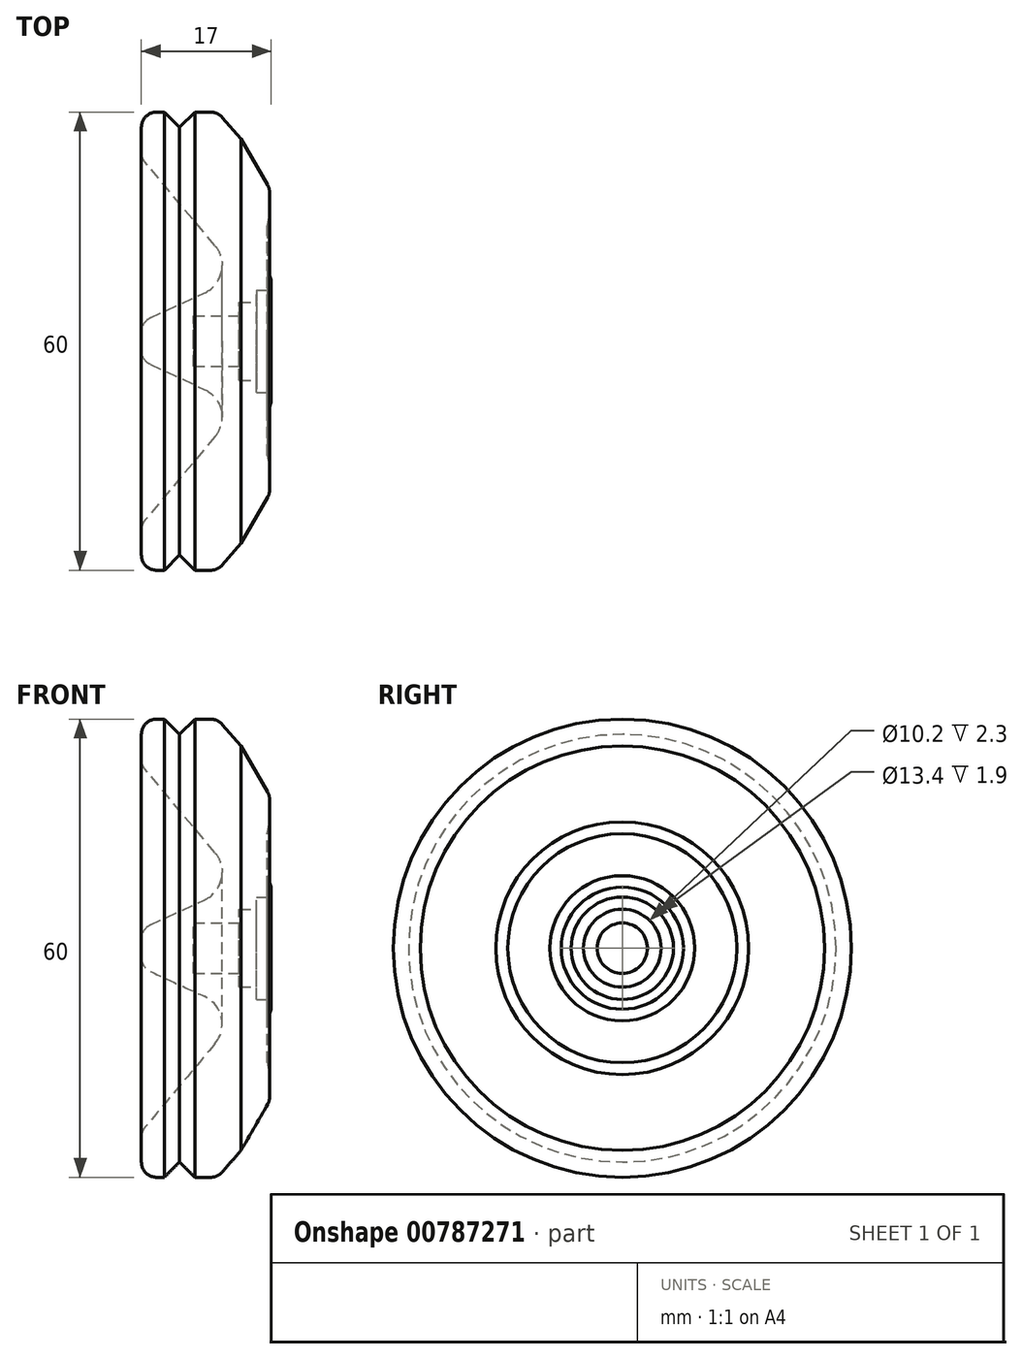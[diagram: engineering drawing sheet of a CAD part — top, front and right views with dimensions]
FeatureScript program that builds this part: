
annotation { "Feature Type Name" : "Feature", "Feature Type Description" : "" }
export const myFeature = defineFeature(function(context is Context, id is Id, definition is map)
    precondition{}
    {
        {
            var Q0;
            Q0=qCreatedBy(makeId("Front.planeOp"),FACE);
            var sketch = newSketch(context, id + "F0", { "sketchPlane" : qUnion([Q0])});
            skLineSegment(sketch, "E0", {"start": v(0, 0) * mm, "end": v(0, 1.22) * mm});
            skLineSegment(sketch, "E1", {"start": v(1.16, 3.04) * mm, "end": v(8.25, 6.3) * mm});
            skLineSegment(sketch, "E2", {"start": v(9.64, 12.5) * mm, "end": v(0.47, 23.44) * mm});
            skLineSegment(sketch, "E3", {"start": v(0, 24.73) * mm, "end": v(0, 28) * mm});
            skLineSegment(sketch, "E4", {"start": v(2, 30) * mm, "end": v(3, 30) * mm});
            skLineSegment(sketch, "E5", {"start": v(3, 30) * mm, "end": v(5, 28) * mm});
            skLineSegment(sketch, "E6", {"start": v(5, 28) * mm, "end": v(7, 30) * mm});
            skLineSegment(sketch, "E7", {"start": v(7, 30) * mm, "end": v(9.09, 30) * mm});
            skLineSegment(sketch, "E8", {"start": v(10.6, 29.31) * mm, "end": v(13.06, 26.48) * mm});
            skLineSegment(sketch, "E9", {"start": v(13.06, 26.48) * mm, "end": v(16.53, 20.46) * mm});
            skLineSegment(sketch, "E10", {"start": v(16.8, 19.46) * mm, "end": v(16.8, 16.55) * mm});
            skLineSegment(sketch, "E11", {"start": v(16.8, 16.55) * mm, "end": v(16.5, 15) * mm});
            skLineSegment(sketch, "E12", {"start": v(16.5, 15) * mm, "end": v(16.5, 9.5) * mm});
            skLineSegment(sketch, "E13", {"start": v(16.5, 9.5) * mm, "end": v(17, 8) * mm});
            skLineSegment(sketch, "E14", {"start": v(17, 8) * mm, "end": v(17, 6.7) * mm});
            skLineSegment(sketch, "E15", {"start": v(17, 6.7) * mm, "end": v(15.1, 6.7) * mm});
            skLineSegment(sketch, "E16", {"start": v(15.1, 6.7) * mm, "end": v(15.1, 5.1) * mm});
            skLineSegment(sketch, "E17", {"start": v(15.1, 5.1) * mm, "end": v(12.8, 5.1) * mm});
            skLineSegment(sketch, "E18", {"start": v(12.8, 5.1) * mm, "end": v(12.8, 3.3) * mm});
            skLineSegment(sketch, "E19", {"start": v(12.8, 3.3) * mm, "end": v(6.8, 3.3) * mm});
            skLineSegment(sketch, "E20", {"start": v(6.8, 3.3) * mm, "end": v(6.8, 0) * mm});
            skLineSegment(sketch, "E21", {"start": v(6.8, 0) * mm, "end": v(0, 0) * mm});
            skPoint(sketch, "E22.visualSharp", {"position": v(0, 30) * mm});
            skArc(sketch, "E22.filletArc", {"start": v(2, 30) * mm, "mid": v(0.59, 29.41) * mm, "end": v(0, 28) * mm});
            skPoint(sketch, "E23.visualSharp", {"position": v(10, 30) * mm});
            skArc(sketch, "E23.filletArc", {"start": v(10.6, 29.31) * mm, "mid": v(9.92, 29.82) * mm, "end": v(9.09, 30) * mm});
            skPoint(sketch, "E24.visualSharp", {"position": v(16.8, 20) * mm});
            skArc(sketch, "E24.filletArc", {"start": v(16.8, 19.46) * mm, "mid": v(16.73, 19.98) * mm, "end": v(16.53, 20.46) * mm});
            skPoint(sketch, "E25.visualSharp", {"position": v(13, 8.5) * mm});
            skArc(sketch, "E25.filletArc", {"start": v(8.25, 6.3) * mm, "mid": v(10.48, 9.07) * mm, "end": v(9.64, 12.5) * mm});
            skPoint(sketch, "E26.visualSharp", {"position": v(0, 2.5) * mm});
            skArc(sketch, "E26.filletArc", {"start": v(1.16, 3.04) * mm, "mid": v(0.32, 2.3) * mm, "end": v(0, 1.22) * mm});
            skPoint(sketch, "E27.visualSharp", {"position": v(0, 24) * mm});
            skArc(sketch, "E27.filletArc", {"start": v(0, 24.73) * mm, "mid": v(0.12, 24.04) * mm, "end": v(0.47, 23.44) * mm});
            skSolve(sketch);
        }
        {
            var Q0;
            Q0=makeQuery(id+"F0.imprint","IMPRINT",FACE,{"disambiguationData":[TD([[makeQuery(id+"F0.imprint","IMPRINT",EDGE,{"derivedFrom":sQuery(id+"F0.wireOp",EDGE,"E0")}),-1.0]])]});
            var Q1;
            Q1=sQuery(id+"F0.wireOp",EDGE,"E21");
            revolve(context, id + "F1", {"surfaceOperationType" : NewSurfaceOperationType.NEW, "entities" : qUnion([Q0]), "axis" : qUnion([Q1]), "revolveType" : RevolveType.FULL});
        }
    });
